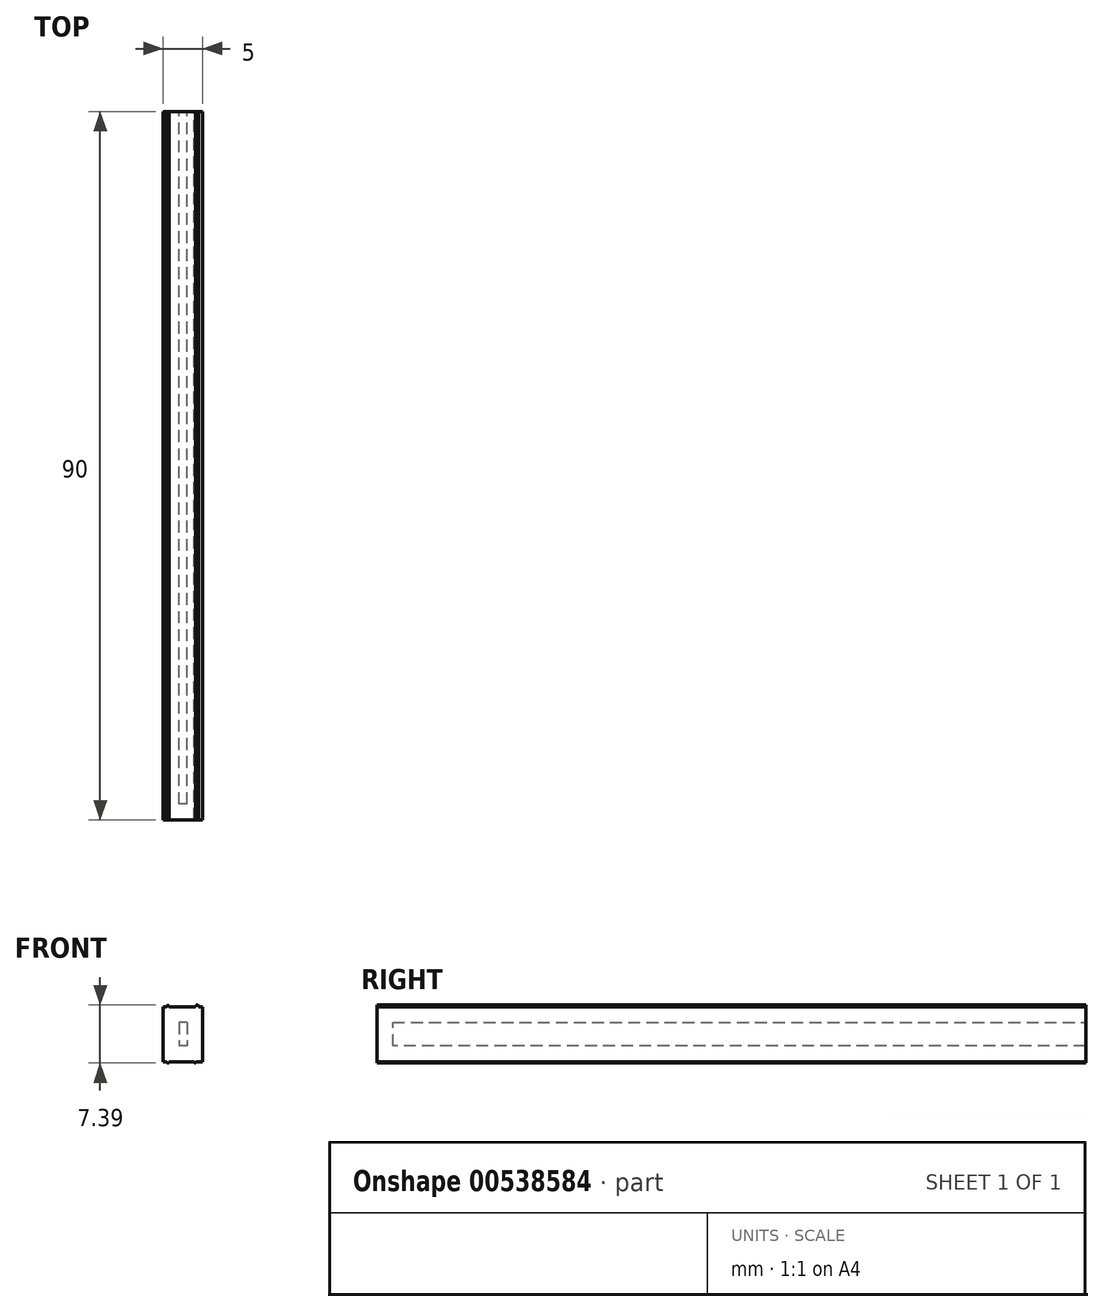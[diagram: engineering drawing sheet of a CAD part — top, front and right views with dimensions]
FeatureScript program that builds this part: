
annotation { "Feature Type Name" : "Feature", "Feature Type Description" : "" }
export const myFeature = defineFeature(function(context is Context, id is Id, definition is map)
    precondition{}
    {
        {
            var Q0;
            Q0=qCreatedBy(makeId("Right.planeOp"),FACE);
            var sketch = newSketch(context, id + "F0", { "sketchPlane" : qUnion([Q0])});
            skLineSegment(sketch, "E0", {"start": v(-31.4, 7) * mm, "end": v(58.6, 7) * mm});
            skLineSegment(sketch, "E1", {"start": v(58.6, 7) * mm, "end": v(58.6, 0) * mm});
            skLineSegment(sketch, "E2", {"start": v(58.6, 0) * mm, "end": v(-31.4, 0) * mm});
            skLineSegment(sketch, "E3", {"start": v(-31.4, 0) * mm, "end": v(-31.4, 7) * mm});
            skSolve(sketch);
        }
        {
            var Q0;
            Q0=makeQuery(id+"F0.imprint","IMPRINT",FACE,{"disambiguationData":[TD([[makeQuery(id+"F0.imprint","IMPRINT",EDGE,{"derivedFrom":sQuery(id+"F0.wireOp",EDGE,"E0")}),-1.0]])]});
            extrude(context, id + "F1", {"entities" : qUnion([Q0]), "depth" : 5 * mm, "offsetDistance" : 25 * mm});
        }
        {
            var Q0;
            Q0=makeQuery(id+"F1.opExtrude","SWEPT_FACE",FACE,{"disambiguationData":[OSD([sQuery(id+"F0.wireOp",EDGE,"E1")])]});
            shell(context, id + "F2", {"entities" : qUnion([Q0]), "thickness" : 2 * mm});
        }
        {
            var Q0;
            Q0=makeQuery(id+"F1.opExtrude","SWEPT_FACE",FACE,{"disambiguationData":[OSD([sQuery(id+"F0.wireOp",EDGE,"E1")])]});
            var sketch = newSketch(context, id + "F3", { "sketchPlane" : qUnion([Q0])});
            skFitSpline(sketch, "E4", {"points": [v(-4.5, 6.83) * mm, v(-4.31, 7.23) * mm, v(-4.12, 6.82) * mm, v(-4.5, 6.83) * mm]});
            skSolve(sketch);
        }
        {
            var Q0;
            Q0 = qSketchRegion(id + "F3", true);
            extrude(context, id + "F4", {"entities" : qUnion([Q0]), "operationType" : NewBodyOperationType.ADD, "oppositeDirection" : true, "depth" : 90 * mm, "offsetDistance" : 25 * mm});
        }
        {
            var Q0;
            Q0=makeQuery(id+"F4.boolean.opBoolean","MERGE",FACE,{"derivedFrom":[makeQuery(id+"F1.opExtrude","SWEPT_FACE",FACE,{"disambiguationData":[OSD([sQuery(id+"F0.wireOp",EDGE,"E1")])]}),makeQuery(id+"F4.opExtrude","CAP_FACE",FACE,{"disambiguationData":[OSD([sQuery(id+"F3.wireOp",EDGE,"E4")])],"isStart":true})]});
            var sketch = newSketch(context, id + "F5", { "sketchPlane" : qUnion([Q0])});
            skFitSpline(sketch, "E5", {"points": [v(-0.72, 6.94) * mm, v(-0.61, 7.2) * mm, v(-0.47, 6.93) * mm, v(-0.72, 6.94) * mm]});
            skSolve(sketch);
        }
        {
            var Q0;
            {var subQ0=sQuery(id+"F5.wireOp",EDGE,"E5");var subQ2=sQuery(id+"F0.wireOp",EDGE,"E1");var subQ3=sQuery(id+"F0.wireOp",EDGE,"E0");var subQ4=makeQuery(id+"F4.boolean.opBoolean","SPLIT",EDGE,{"disambiguationData":[TD([makeQuery(id+"F1.opExtrude","CAP_FACE",FACE,{"disambiguationData":[OSD([subQ3,subQ2,sQuery(id+"F0.wireOp",EDGE,"E2"),sQuery(id+"F0.wireOp",EDGE,"E3")])],"isStart":true})])],"derivedFrom":makeQuery(id+"F1.opExtrude","SWEPT_EDGE",EDGE,{"disambiguationData":[OSD([subQ3,subQ2])]})});var subQ5=makeQuery(id+"F5.imprint","INTERSECT",VERTEX,{"disambiguationData":[OD(0.0)],"derivedFrom":[subQ4,subQ0]});Q0=makeQuery(id+"F5.imprint","IMPRINT",FACE,{"disambiguationData":[TD([[makeQuery(id+"F5.imprint","IMPRINT",EDGE,{"disambiguationData":[TD([[subQ5,1.0]])],"derivedFrom":subQ0}),-1.0]])]});}
            extrude(context, id + "F6", {"entities" : qUnion([Q0]), "operationType" : NewBodyOperationType.ADD, "oppositeDirection" : true, "depth" : 90 * mm, "offsetDistance" : 25 * mm});
        }
        {
            var Q0;
            {var subQ0=sQuery(id+"F0.wireOp",EDGE,"E1");Q0=makeQuery(id+"F6.boolean.opBoolean","MERGE",FACE,{"derivedFrom":[makeQuery(id+"F4.boolean.opBoolean","MERGE",FACE,{"derivedFrom":[makeQuery(id+"F1.opExtrude","SWEPT_FACE",FACE,{"disambiguationData":[OSD([subQ0])]}),makeQuery(id+"F4.opExtrude","CAP_FACE",FACE,{"disambiguationData":[OSD([sQuery(id+"F3.wireOp",EDGE,"E4")])],"isStart":true})]}),makeQuery(id+"F6.opExtrude","CAP_FACE",FACE,{"disambiguationData":[OSD([sQuery(id+"F0.wireOp",EDGE,"E0"),subQ0,sQuery(id+"F5.wireOp",EDGE,"E5")])],"isStart":true})]});}
            var sketch = newSketch(context, id + "F7", { "sketchPlane" : qUnion([Q0])});
            skFitSpline(sketch, "E6", {"points": [v(-0.46, 0) * mm, v(-0.59, -0.16) * mm, v(-0.74, 0) * mm, v(-0.46, 0) * mm]});
            skSolve(sketch);
        }
        {
            var Q0;
            {var subQ3=sQuery(id+"F0.wireOp",EDGE,"E1");var subQ12=makeQuery(id+"F1.opExtrude","CAP_EDGE",EDGE,{"disambiguationData":[OSD([subQ3])],"isStart":true});Q0=makeQuery(id+"F7.imprint","IMPRINT",FACE,{"disambiguationData":[TD([[makeQuery(id+"F7.imprint","IMPRINT",EDGE,{"derivedFrom":subQ12}),-1.0]])]});}
            var sketch = newSketch(context, id + "F8", { "sketchPlane" : qUnion([Q0])});
            skFitSpline(sketch, "E7", {"points": [v(-3.92, 0) * mm, v(-4.01, -0.12) * mm, v(-4.17, 0) * mm, v(-3.92, 0) * mm]});
            skSolve(sketch);
        }
        {
            var Q0;
            {var subQ0=sQuery(id+"F7.wireOp",EDGE,"E6");var subQ1=makeQuery(id+"F1.opExtrude","SWEPT_EDGE",EDGE,{"disambiguationData":[OSD([sQuery(id+"F0.wireOp",EDGE,"E1"),sQuery(id+"F0.wireOp",EDGE,"E2")])]});var subQ2=makeQuery(id+"F7.imprint","INTERSECT",VERTEX,{"disambiguationData":[OD(0.0)],"derivedFrom":[subQ1,subQ0]});Q0=makeQuery(id+"F7.imprint","IMPRINT",FACE,{"disambiguationData":[TD([[makeQuery(id+"F7.imprint","IMPRINT",EDGE,{"disambiguationData":[TD([[subQ2,-1.0]])],"derivedFrom":subQ0}),-1.0]])]});}
            var Q1;
            {var subQ0=sQuery(id+"F8.wireOp",EDGE,"E7");var subQ1=sQuery(id+"F0.wireOp",EDGE,"E1");var subQ2=makeQuery(id+"F1.opExtrude","SWEPT_EDGE",EDGE,{"disambiguationData":[OSD([subQ1,sQuery(id+"F0.wireOp",EDGE,"E2")])]});var subQ3=makeQuery(id+"F7.imprint","IMPRINT",EDGE,{"disambiguationData":[TD([[makeQuery(id+"F7.imprint","INTERSECT",VERTEX,{"derivedFrom":[subQ2,makeQuery(id+"F1.opExtrude","CAP_EDGE",EDGE,{"disambiguationData":[OSD([subQ1])],"isStart":false})]}),-1.0]])],"derivedFrom":subQ2});var subQ4=makeQuery(id+"F8.imprint","INTERSECT",VERTEX,{"disambiguationData":[OD(0.0)],"derivedFrom":[subQ3,subQ0]});Q1=makeQuery(id+"F8.imprint","IMPRINT",FACE,{"disambiguationData":[TD([[makeQuery(id+"F8.imprint","IMPRINT",EDGE,{"disambiguationData":[TD([[subQ4,1.0]])],"derivedFrom":subQ0}),-1.0]])]});}
            extrude(context, id + "F9", {"entities" : qUnion([Q0, Q1]), "operationType" : NewBodyOperationType.ADD, "oppositeDirection" : true, "depth" : 90 * mm, "offsetDistance" : 25 * mm});
        }
    });
